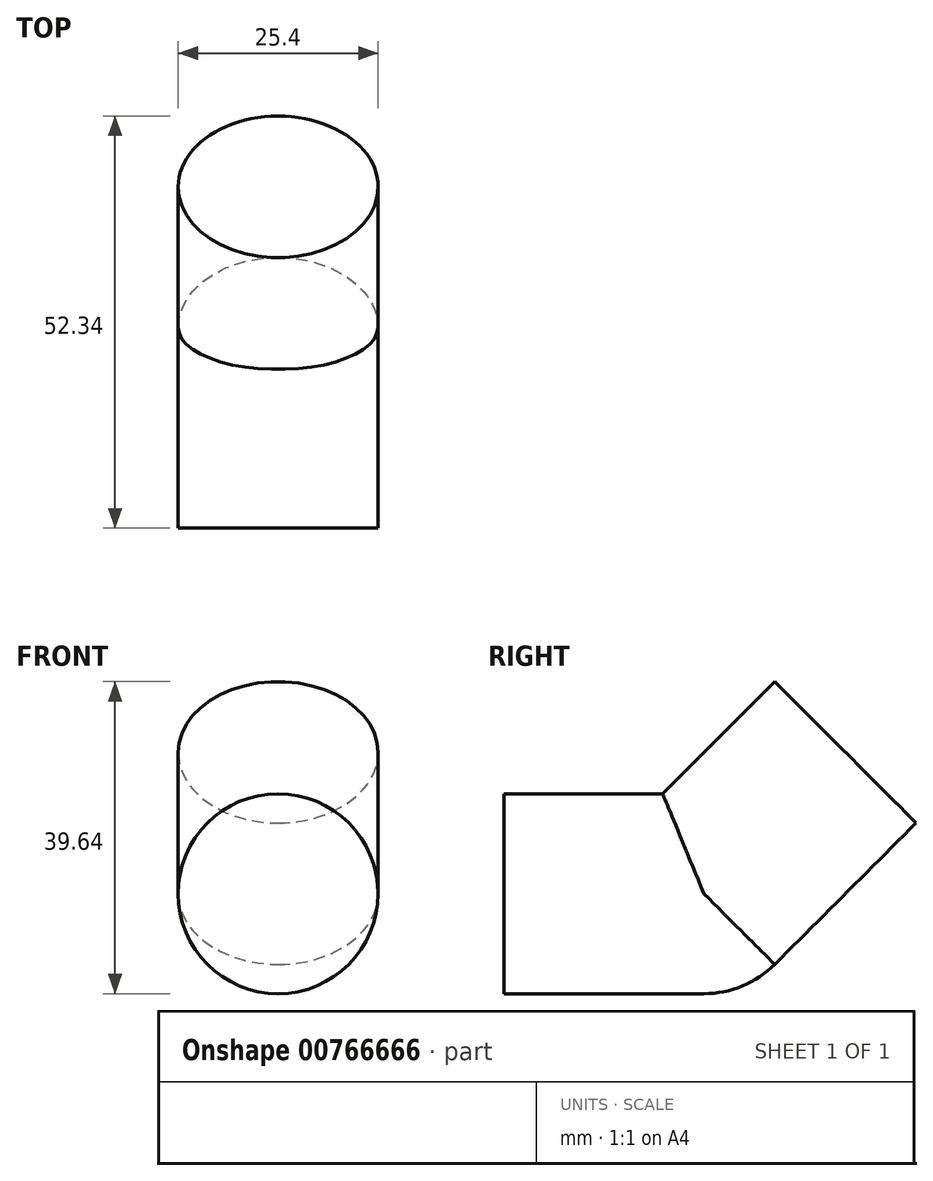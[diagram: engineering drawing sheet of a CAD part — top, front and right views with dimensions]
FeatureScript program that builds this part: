
annotation { "Feature Type Name" : "Feature", "Feature Type Description" : "" }
export const myFeature = defineFeature(function(context is Context, id is Id, definition is map)
    precondition{}
    {
        {
            var Q0;
            Q0=qCreatedBy(makeId("Right.planeOp"),FACE);
            var sketch = newSketch(context, id + "F0", { "sketchPlane" : qUnion([Q0])});
            skLineSegment(sketch, "E0", {"start": v(0, 0) * mm, "end": v(17.96, 17.96) * mm});
            skSolve(sketch);
        }
        {
            var Q0;
            Q0=sQuery(id+"F0.wireOp",EDGE,"E0");
            extrude(context, id + "F1", {"bodyType" : ToolBodyType.SURFACE, "surfaceEntities" : qUnion([Q0]), "depth" : 12.7 * mm, "offsetDistance" : 25.4 * mm});
        }
        {
            var Q0;
            Q0 = qSketchRegion(id + "F0", true);
            var Q1;
            Q1=makeQuery(id+"F1.opExtrude","SWEPT_FACE",FACE,{"disambiguationData":[OSD([sQuery(id+"F0.wireOp",EDGE,"E0")])]});
            var Q2;
            Q2=makeQuery(id+"F1.opExtrude","CAP_EDGE",EDGE,{"disambiguationData":[OSD([sQuery(id+"F0.wireOp",EDGE,"E0")])],"isStart":true});
            revolve(context, id + "F2", {"surfaceOperationType" : NewSurfaceOperationType.NEW, "entities" : qUnion([Q0, Q1]), "axis" : qUnion([Q2]), "revolveType" : RevolveType.FULL});
        }
        {
            var Q0;
            Q0=qCreatedBy(makeId("Right.planeOp"),FACE);
            var sketch = newSketch(context, id + "F3", { "sketchPlane" : qUnion([Q0])});
            skCircle(sketch, "E1", {"center": v(0, 0) * mm, "radius": 12.7 * mm});
            skLineSegment(sketch, "E2", {"start": v(0, 26.43) * mm, "end": v(0, -30.55) * mm});
            skSolve(sketch);
        }
        {
            var Q0;
            {var subQ0=sQuery(id+"F3.wireOp",EDGE,"E2");var subQ1=sQuery(id+"F3.wireOp",EDGE,"E1");var subQ2=makeQuery(id+"F3.imprint","INTERSECT",VERTEX,{"disambiguationData":[OD(0.0)],"derivedFrom":[subQ1,subQ0]});Q0=makeQuery(id+"F3.imprint","IMPRINT",FACE,{"disambiguationData":[TD([[makeQuery(id+"F3.imprint","IMPRINT",EDGE,{"disambiguationData":[TD([[subQ2,-1.0]])],"derivedFrom":subQ1}),1.0]])]});}
            var Q1;
            Q1=sQuery(id+"F3.wireOp",EDGE,"E2");
            revolve(context, id + "F4", {"operationType" : NewBodyOperationType.ADD, "surfaceOperationType" : NewSurfaceOperationType.NEW, "entities" : qUnion([Q0]), "axis" : qUnion([Q1]), "revolveType" : RevolveType.FULL});
        }
        {
            var Q0;
            Q0=qCreatedBy(makeId("Front.planeOp"),FACE);
            var sketch = newSketch(context, id + "F5", { "sketchPlane" : qUnion([Q0])});
            skCircle(sketch, "E3", {"center": v(0, 0) * mm, "radius": 12.7 * mm});
            skSolve(sketch);
        }
        {
            var Q0;
            Q0 = qSketchRegion(id + "F5", true);
            extrude(context, id + "F6", {"entities" : qUnion([Q0]), "operationType" : NewBodyOperationType.ADD, "depth" : 25.4 * mm, "offsetDistance" : 25.4 * mm});
        }
    });
